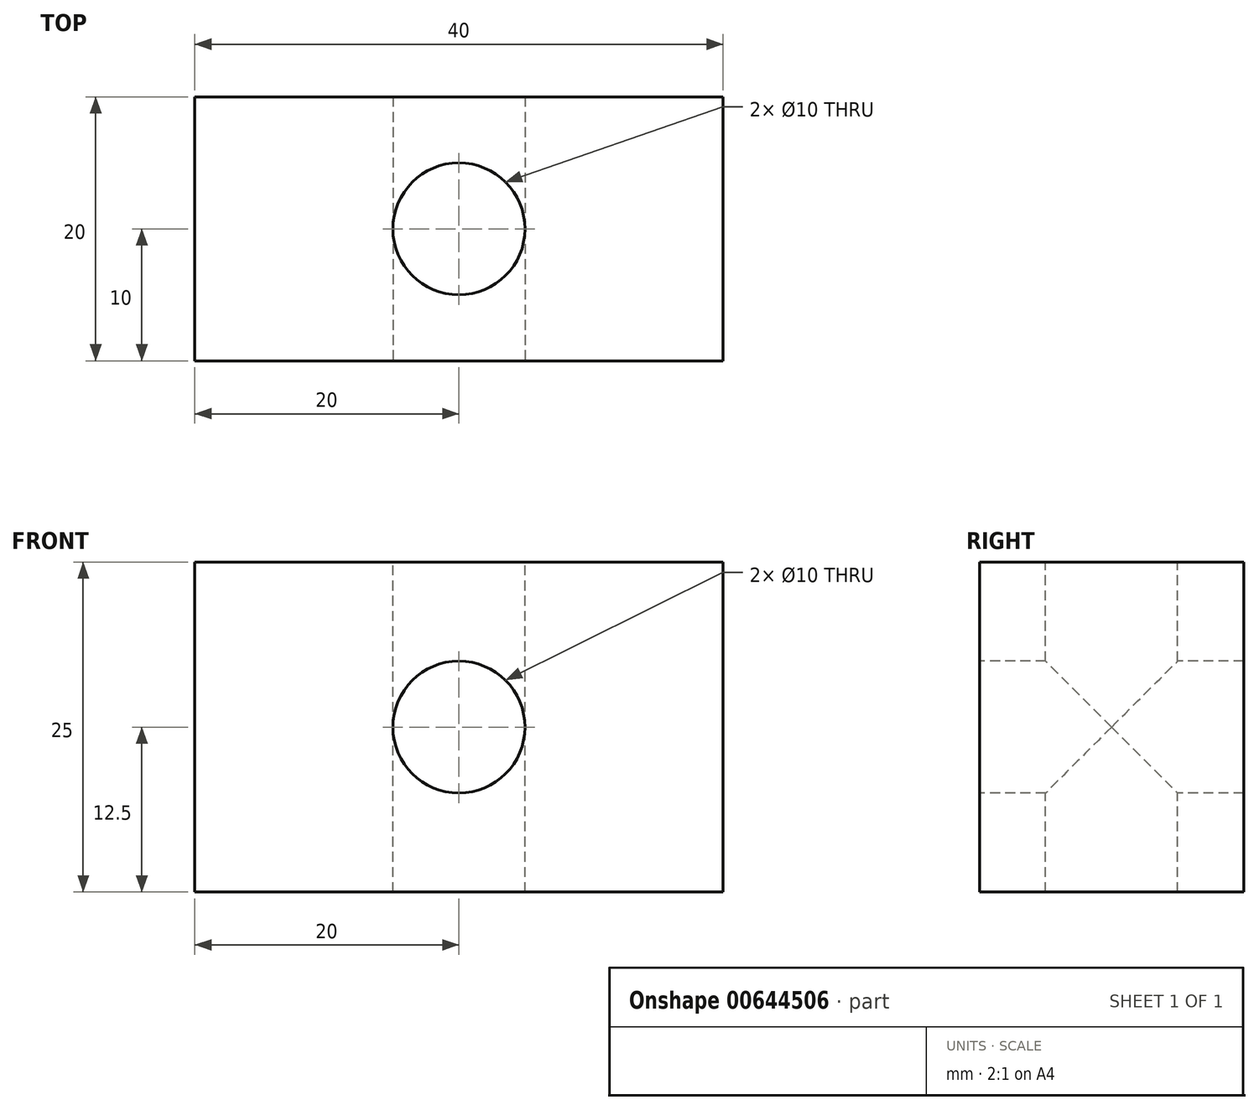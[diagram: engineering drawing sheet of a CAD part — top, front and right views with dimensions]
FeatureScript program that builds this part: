
annotation { "Feature Type Name" : "Feature", "Feature Type Description" : "" }
export const myFeature = defineFeature(function(context is Context, id is Id, definition is map)
    precondition{}
    {
        {
            var Q0;
            Q0=qCreatedBy(makeId("Top.planeOp"),FACE);
            var sketch = newSketch(context, id + "F0", { "sketchPlane" : qUnion([Q0])});
            skLineSegment(sketch, "E0.bottom", {"start": v(0, 0) * mm, "end": v(40, 0) * mm});
            skLineSegment(sketch, "E0.top", {"start": v(0, 20) * mm, "end": v(40, 20) * mm});
            skLineSegment(sketch, "E0.left", {"start": v(0, 0) * mm, "end": v(0, 20) * mm});
            skLineSegment(sketch, "E0.right", {"start": v(40, 0) * mm, "end": v(40, 20) * mm});
            skSolve(sketch);
        }
        {
            var Q0;
            Q0 = qSketchRegion(id + "F0", true);
            extrude(context, id + "F1", {"entities" : qUnion([Q0]), "depth" : 25 * mm, "offsetDistance" : 25 * mm});
        }
        {
            var Q0;
            Q0=makeQuery(id+"F1.opExtrude","CAP_FACE",FACE,{"disambiguationData":[OSD([sQuery(id+"F0.wireOp",EDGE,"E0.bottom"),sQuery(id+"F0.wireOp",EDGE,"E0.top"),sQuery(id+"F0.wireOp",EDGE,"E0.left"),sQuery(id+"F0.wireOp",EDGE,"E0.right")])],"isStart":false});
            var sketch = newSketch(context, id + "F2", { "sketchPlane" : qUnion([Q0])});
            skCircle(sketch, "E1", {"center": v(20, 10) * mm, "radius": 5 * mm});
            skPoint(sketch, "E1.centerSnap0", {"position": v(0, 10) * mm});
            skPoint(sketch, "E1.centerSnap1", {"position": v(20, 20) * mm});
            skSolve(sketch);
        }
        {
            var Q0;
            Q0 = qSketchRegion(id + "F2", true);
            extrude(context, id + "F3", {"entities" : qUnion([Q0]), "operationType" : NewBodyOperationType.REMOVE, "oppositeDirection" : true, "depth" : 25 * mm, "offsetDistance" : 25 * mm});
        }
        {
            var Q0;
            Q0=makeQuery(id+"F1.opExtrude","SWEPT_FACE",FACE,{"disambiguationData":[OSD([sQuery(id+"F0.wireOp",EDGE,"E0.bottom")])]});
            var sketch = newSketch(context, id + "F4", { "sketchPlane" : qUnion([Q0])});
            skCircle(sketch, "E2", {"center": v(20, 12.5) * mm, "radius": 5 * mm});
            skPoint(sketch, "E2.centerSnap0", {"position": v(40, 12.5) * mm});
            skPoint(sketch, "E2.centerSnap1", {"position": v(20, 25) * mm});
            skSolve(sketch);
        }
        {
            var Q0;
            Q0 = qSketchRegion(id + "F4", true);
            extrude(context, id + "F5", {"entities" : qUnion([Q0]), "operationType" : NewBodyOperationType.REMOVE, "oppositeDirection" : true, "depth" : 25 * mm, "offsetDistance" : 25 * mm});
        }
    });
